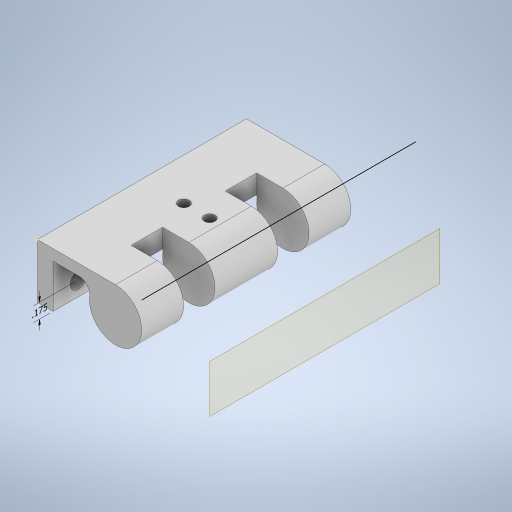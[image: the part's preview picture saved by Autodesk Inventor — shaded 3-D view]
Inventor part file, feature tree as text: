
AUTODESK INVENTOR PART (.ipt)
format: ipt  version: 2024.2 (Build 282272000, 272)  size: 347,648 bytes
history: native  units: in
note: dims shown in document units (in); Inventor stores cm internally (conversion verified against a paired STEP export)
features: sketch x6, extrude x5, other x2, plane x1
ambient origin geometry x8: Origin, YZ Plane, XZ Plane, XY Plane, X Axis, Y Axis, Z Axis, Center Point
bodies: Solid1 (feature_tree)
feature tree (14):
  other  "Annotations"
  extrude  "Extrusion1"  Depth=0.65in
  extrude  "Extrusion2"  Depth=0.3937in
  extrude  "Extrusion3"  Depth=0.13in
  sketch  "Sketch4"  dims[d15=0.04in d16=0.0in d17=0.935in]
  plane  "Work Plane1"
  extrude  "Extrusion4"  Depth=0.935in
  extrude  "Extrusion5"  Depth=0.125in
  sketch  "Sketch1"  dims[d0=2.5in d1=0.65in]
  sketch  "Sketch2"  dims[d4=2.7559in d6=0.3149in d7=0.3937in d9=1.0in d11=0.3in]
  sketch  "Sketch3"  dims[d12=0.1875in d13=0.0in d14=0.13in]
  sketch  "Sketch6"  dims[d18=0.625in d19=0.125in]
  sketch  "Sketch7"  dims[d20=2.5in d21=0.0in d25=2.0in d26=0.375in d27=0.5in d28=0.375in d29=0.5in d30=0.0in d31=0.0in d32=0.625in d33=0.625in d34=0.129in d35=1.25in d36=0.125in d37=0.129in d38=0.0in d39=0.0in d23=0.0278in d24=0.175in]
  other  "Linear Dimension 1"
